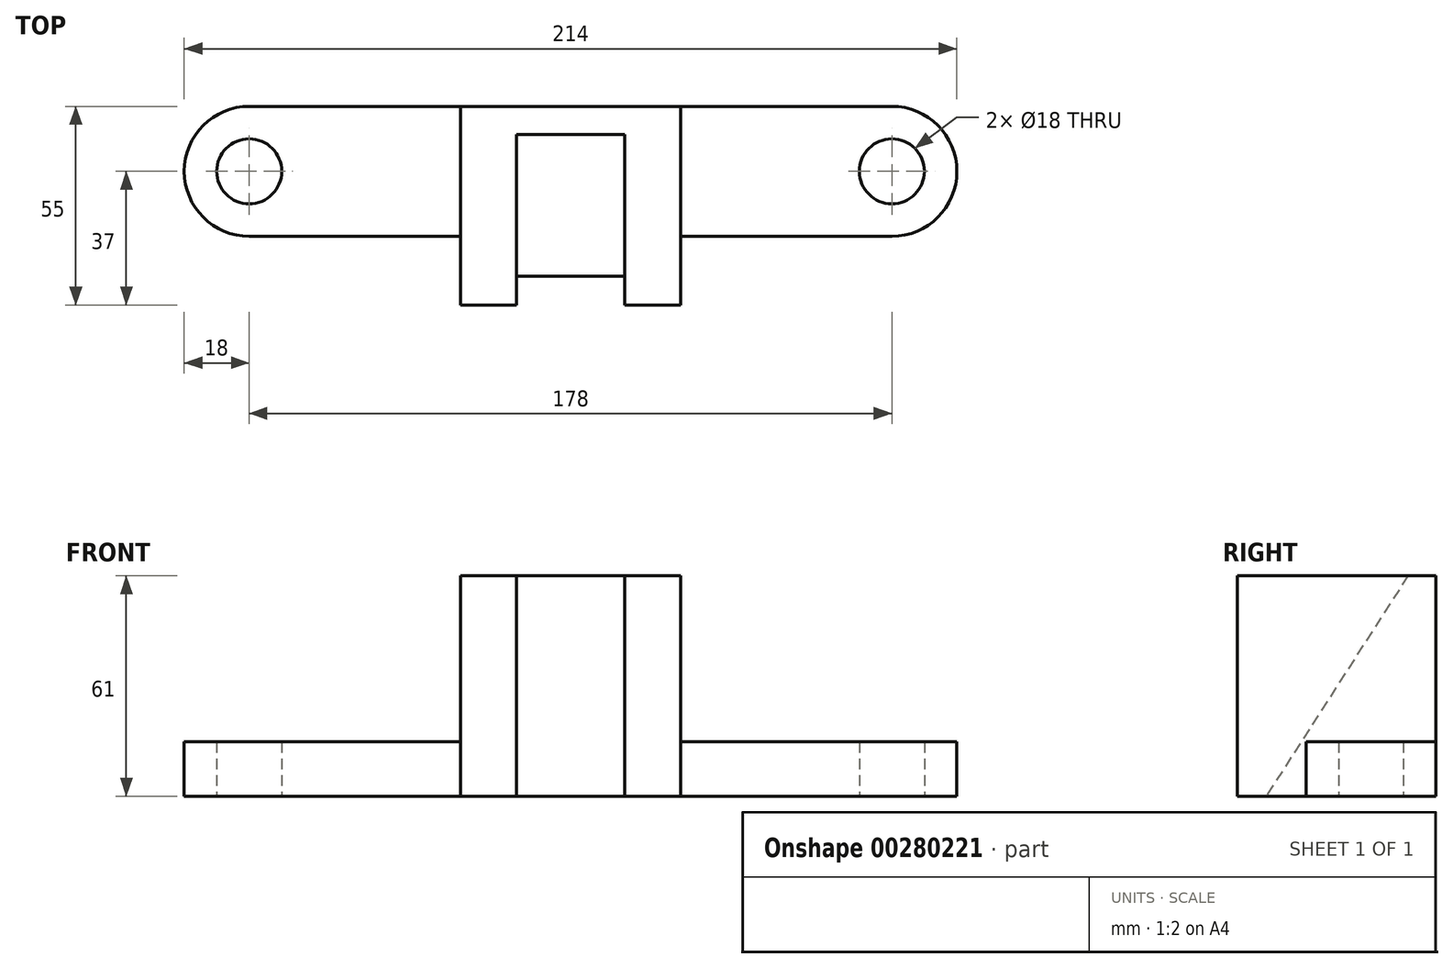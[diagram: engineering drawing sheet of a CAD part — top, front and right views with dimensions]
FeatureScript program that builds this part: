
annotation { "Feature Type Name" : "Feature", "Feature Type Description" : "" }
export const myFeature = defineFeature(function(context is Context, id is Id, definition is map)
    precondition{}
    {
        {
            var Q0;
            Q0=qCreatedBy(makeId("Top.planeOp"),FACE);
            var sketch = newSketch(context, id + "F0", { "sketchPlane" : qUnion([Q0])});
            skLineSegment(sketch, "E0", {"start": v(-30.5, 30.65) * mm, "end": v(30.5, 30.65) * mm});
            skLineSegment(sketch, "E1", {"start": v(0, 22.9) * mm, "end": v(15, 22.9) * mm});
            skLineSegment(sketch, "E2", {"start": v(15, 22.9) * mm, "end": v(15, -24.35) * mm});
            skLineSegment(sketch, "E3", {"start": v(15, -24.35) * mm, "end": v(30.5, -24.35) * mm});
            skLineSegment(sketch, "E4", {"start": v(30.5, -24.35) * mm, "end": v(30.5, 30.65) * mm});
            skLineSegment(sketch, "E5.trimOffspring", {"start": v(15, -16.35) * mm, "end": v(-15, -16.35) * mm});
            skLineSegment(sketch, "E6.MirrorCS", {"start": v(30.5, 30.65) * mm, "end": v(-30.5, 30.65) * mm});
            skPoint(sketch, "E7.orphan", {"position": v(-30.5, 30.65) * mm});
            skLineSegment(sketch, "E8.MirrorCS", {"start": v(-15, 22.9) * mm, "end": v(-15, -24.35) * mm});
            skLineSegment(sketch, "E9.MirrorCS", {"start": v(-30.5, -24.35) * mm, "end": v(-30.5, 30.65) * mm});
            skLineSegment(sketch, "E10.MirrorCS", {"start": v(-15, -24.35) * mm, "end": v(-30.5, -24.35) * mm});
            skPoint(sketch, "E11.MirrorCS.end.orphan", {"position": v(-30.5, -5.35) * mm});
            skLineSegment(sketch, "E12.MirrorCS", {"start": v(0, 22.9) * mm, "end": v(-15, 22.9) * mm});
            skPoint(sketch, "E13.end.orphan", {"position": v(30.5, -5.35) * mm});
            skLineSegment(sketch, "E14", {"start": v(30.5, 30.65) * mm, "end": v(89, 30.65) * mm});
            skLineSegment(sketch, "E15", {"start": v(89, -5.35) * mm, "end": v(30.5, -5.35) * mm});
            skCircle(sketch, "E16", {"center": v(89, 12.65) * mm, "radius": 9 * mm});
            skArc(sketch, "E17", {"start": v(89, -5.35) * mm, "mid": v(107, 12.65) * mm, "end": v(89, 30.65) * mm});
            skLineSegment(sketch, "E18.MirrorCS", {"start": v(-30.5, 30.65) * mm, "end": v(-89, 30.65) * mm});
            skArc(sketch, "E19.MirrorCS", {"start": v(-89, -5.35) * mm, "mid": v(-107, 12.65) * mm, "end": v(-89, 30.65) * mm});
            skLineSegment(sketch, "E20.MirrorCS", {"start": v(-89, -5.35) * mm, "end": v(-30.5, -5.35) * mm});
            skCircle(sketch, "E21.MirrorC", {"center": v(-89, 12.65) * mm, "radius": 9 * mm});
            skSolve(sketch);
        }
        {
            var Q0;
            {var subQ9=sQuery(id+"F0.wireOp",EDGE,"E1");Q0=makeQuery(id+"F0.imprint","IMPRINT",FACE,{"disambiguationData":[TD([[makeQuery(id+"F0.imprint","IMPRINT",EDGE,{"derivedFrom":subQ9}),1.0]])]});}
            extrude(context, id + "F1", {"entities" : qUnion([Q0]), "depth" : 61 * mm});
        }
        {
            var Q0;
            {var subQ0=sQuery(id+"F0.wireOp",EDGE,"E14");Q0=makeQuery(id+"F0.imprint","IMPRINT",FACE,{"disambiguationData":[TD([[makeQuery(id+"F0.imprint","IMPRINT",EDGE,{"derivedFrom":subQ0}),-1.0]])]});}
            var Q1;
            {var subQ0=sQuery(id+"F0.wireOp",EDGE,"E18.MirrorCS");Q1=makeQuery(id+"F0.imprint","IMPRINT",FACE,{"disambiguationData":[TD([[makeQuery(id+"F0.imprint","IMPRINT",EDGE,{"derivedFrom":subQ0}),1.0]])]});}
            extrude(context, id + "F2", {"entities" : qUnion([Q0, Q1]), "operationType" : NewBodyOperationType.ADD, "depth" : 15 * mm});
        }
        {
            var Q0;
            Q0=makeQuery(id+"F1.opExtrude","SWEPT_FACE",FACE,{"disambiguationData":[OSD([sQuery(id+"F0.wireOp",EDGE,"E8.MirrorCS")])]});
            var sketch = newSketch(context, id + "F3", { "sketchPlane" : qUnion([Q0])});
            skLineSegment(sketch, "E22", {"start": v(-24.35, 61) * mm, "end": v(22.9, 61) * mm});
            skLineSegment(sketch, "E23", {"start": v(22.9, 61) * mm, "end": v(-16.35, 0) * mm});
            skLineSegment(sketch, "E24", {"start": v(-16.35, 0) * mm, "end": v(-24.35, 0) * mm});
            skLineSegment(sketch, "E25", {"start": v(-24.35, 0) * mm, "end": v(-24.35, 61) * mm});
            skLineSegment(sketch, "E26", {"start": v(-16.35, 0) * mm, "end": v(22.9, 0) * mm});
            skLineSegment(sketch, "E27", {"start": v(22.9, 0) * mm, "end": v(22.9, 61) * mm});
            skSolve(sketch);
        }
        {
            var Q0;
            Q0=makeQuery(id+"F3.imprint","IMPRINT",FACE,{"disambiguationData":[TD([[makeQuery(id+"F3.imprint","IMPRINT",EDGE,{"derivedFrom":sQuery(id+"F3.wireOp",EDGE,"E23")}),1.0]])]});
            extrude(context, id + "F4", {"entities" : qUnion([Q0]), "operationType" : NewBodyOperationType.ADD, "depth" : 30 * mm});
        }
    });
